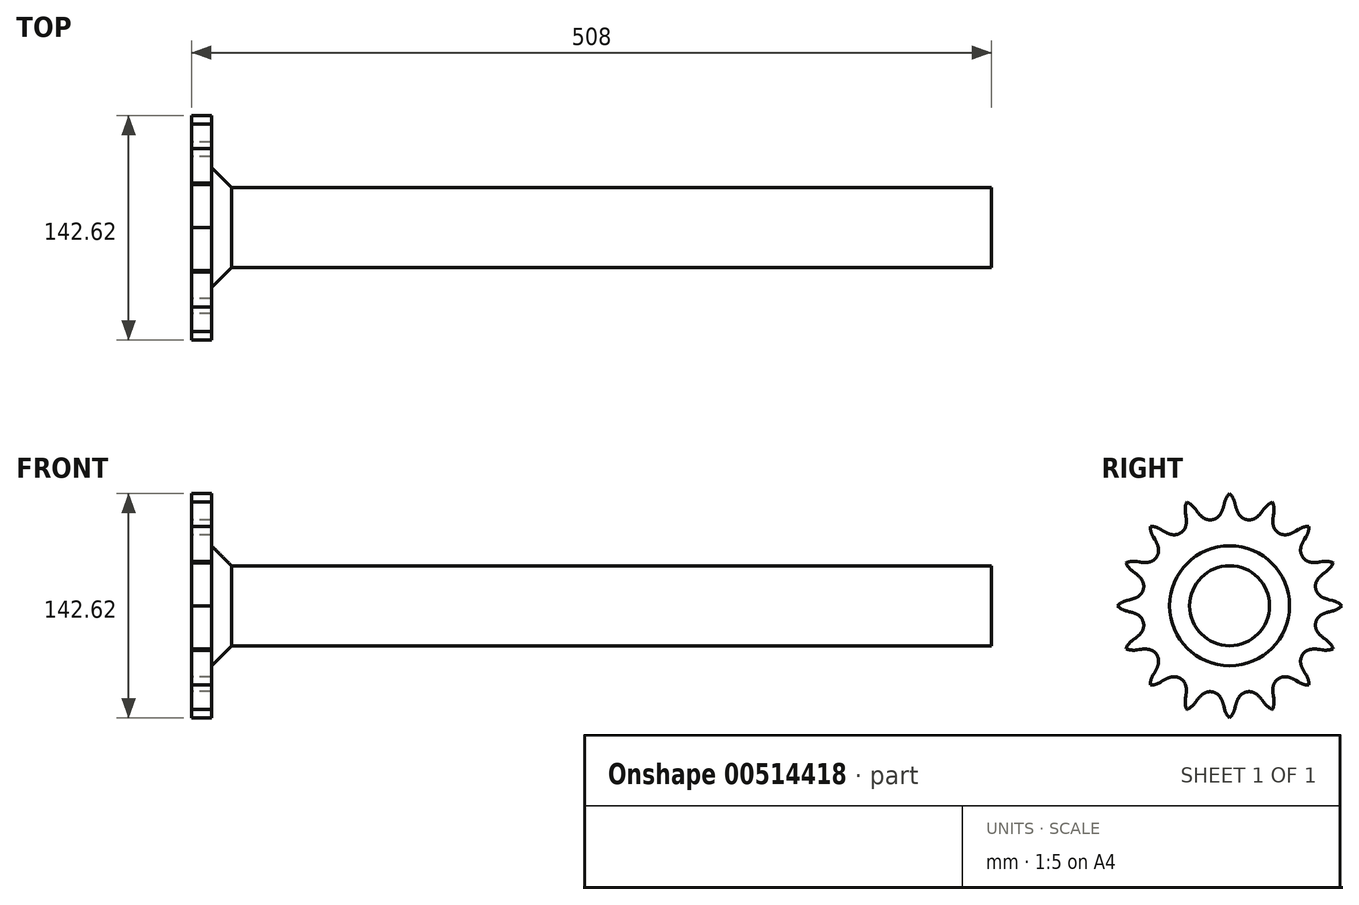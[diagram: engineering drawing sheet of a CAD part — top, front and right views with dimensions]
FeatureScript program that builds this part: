
annotation { "Feature Type Name" : "Feature", "Feature Type Description" : "" }
export const myFeature = defineFeature(function(context is Context, id is Id, definition is map)
    precondition{}
    {
        {
            var Q0;
            Q0=qCreatedBy(makeId("Front.planeOp"),FACE);
            var sketch = newSketch(context, id + "F0", { "sketchPlane" : qUnion([Q0])});
            skLineSegment(sketch, "E0", {"start": v(0, 0) * mm, "end": v(55.03, 0) * mm, "construction": true});
            skLineSegment(sketch, "E1.bottom", {"start": v(0, 25.4) * mm, "end": v(12.7, 25.4) * mm});
            skLineSegment(sketch, "E1.top", {"start": v(0, 76.2) * mm, "end": v(12.7, 76.2) * mm});
            skLineSegment(sketch, "E1.left", {"start": v(0, 25.4) * mm, "end": v(0, 76.2) * mm});
            skLineSegment(sketch, "E1.right", {"start": v(12.7, 25.4) * mm, "end": v(12.7, 76.2) * mm});
            skLineSegment(sketch, "E2.MirrorCS", {"start": v(12.7, -25.4) * mm, "end": v(12.7, -76.2) * mm});
            skLineSegment(sketch, "E3.MirrorCS", {"start": v(0, -25.4) * mm, "end": v(0, -76.2) * mm});
            skLineSegment(sketch, "E4.MirrorCS", {"start": v(0, -76.2) * mm, "end": v(12.7, -76.2) * mm});
            skLineSegment(sketch, "E5.MirrorCS", {"start": v(0, -25.4) * mm, "end": v(12.7, -25.4) * mm});
            skLineSegment(sketch, "E6.bottom", {"start": v(0, 38.1) * mm, "end": v(25.4, 38.1) * mm});
            skLineSegment(sketch, "E6.top", {"start": v(0, 25.4) * mm, "end": v(25.4, 25.4) * mm});
            skLineSegment(sketch, "E6.left", {"start": v(0, 38.1) * mm, "end": v(0, 25.4) * mm});
            skLineSegment(sketch, "E6.right", {"start": v(25.4, 38.1) * mm, "end": v(25.4, 25.4) * mm});
            skLineSegment(sketch, "E7.MirrorCS", {"start": v(25.4, -38.1) * mm, "end": v(25.4, -25.4) * mm});
            skLineSegment(sketch, "E8.MirrorCS", {"start": v(0, -38.1) * mm, "end": v(0, -25.4) * mm});
            skLineSegment(sketch, "E9.MirrorCS", {"start": v(0, -25.4) * mm, "end": v(25.4, -25.4) * mm});
            skLineSegment(sketch, "E10.MirrorCS", {"start": v(0, -38.1) * mm, "end": v(25.4, -38.1) * mm});
            skSolve(sketch);
        }
        {
            var Q0;
            Q0 = qSketchRegion(id + "F0", true);
            var Q1;
            Q1=sQuery(id+"F0.wireOp",EDGE,"E0");
            revolve(context, id + "F1", {"entities" : qUnion([Q0]), "axis" : qUnion([Q1]), "revolveType" : RevolveType.FULL});
        }
        {
            var Q0;
            Q0=makeQuery(id+"F1.opRevolve","SWEPT_FACE",FACE,{"disambiguationData":[OSD([sQuery(id+"F0.wireOp",EDGE,"E3.MirrorCS"),sQuery(id+"F0.wireOp",EDGE,"E8.MirrorCS")])]});
            var sketch = newSketch(context, id + "F2", { "sketchPlane" : qUnion([Q0])});
            skCircle(sketch, "E11", {"center": v(0, 0) * mm, "radius": 25.4 * mm});
            skSolve(sketch);
        }
        {
            var Q0;
            Q0=makeQuery(id+"F2.imprint","IMPRINT",FACE,{"disambiguationData":[TD([[makeQuery(id+"F2.imprint","IMPRINT",EDGE,{"derivedFrom":sQuery(id+"F2.wireOp",EDGE,"E11")}),1.0]])]});
            extrude(context, id + "F3", {"entities" : qUnion([Q0]), "oppositeDirection" : true, "depth" : 508 * mm, "offsetDistance" : 25.4 * mm});
        }
        {
            var Q0;
            Q0=makeQuery(id+"F3.opExtrude","SWEPT_BODY",BODY,{"disambiguationData":[OSD([sQuery(id+"F2.wireOp",EDGE,"E11")])]});
            var Q1;
            Q1=makeQuery(id+"F1.opRevolve","SWEPT_BODY",BODY,{"disambiguationData":[OSD([sQuery(id+"F0.wireOp",EDGE,"E2.MirrorCS"),sQuery(id+"F0.wireOp",EDGE,"E3.MirrorCS"),sQuery(id+"F0.wireOp",EDGE,"E4.MirrorCS"),sQuery(id+"F0.wireOp",EDGE,"E7.MirrorCS"),sQuery(id+"F0.wireOp",EDGE,"E8.MirrorCS"),sQuery(id+"F0.wireOp",EDGE,"E9.MirrorCS"),sQuery(id+"F0.wireOp",EDGE,"E10.MirrorCS")])]});
            var Q2;
            Q2=makeQuery(id+"F1.opRevolve","SWEPT_BODY",BODY,{"disambiguationData":[OSD([sQuery(id+"F0.wireOp",EDGE,"E6.bottom"),sQuery(id+"F0.wireOp",EDGE,"E6.top"),sQuery(id+"F0.wireOp",EDGE,"E6.right"),sQuery(id+"F0.wireOp",EDGE,"E1.bottom"),sQuery(id+"F0.wireOp",EDGE,"E1.top"),sQuery(id+"F0.wireOp",EDGE,"E1.left"),sQuery(id+"F0.wireOp",EDGE,"E1.right")])]});
            booleanBodies(context, id + "F4", {"operationType" : BooleanOperationType.UNION, "tools" : qUnion([Q0, Q1, Q2])});
        }
        {
            var Q0;
            Q0=makeQuery(id+"F4.opBoolean","MERGE",FACE,{"derivedFrom":[makeQuery(id+"F1.opRevolve","SWEPT_FACE",FACE,{"disambiguationData":[OSD([sQuery(id+"F0.wireOp",EDGE,"E3.MirrorCS"),sQuery(id+"F0.wireOp",EDGE,"E8.MirrorCS")])]}),makeQuery(id+"F3.opExtrude","CAP_FACE",FACE,{"disambiguationData":[OSD([sQuery(id+"F2.wireOp",EDGE,"E11")])],"isStart":true})]});
            var sketch = newSketch(context, id + "F5", { "sketchPlane" : qUnion([Q0])});
            skCircle(sketch, "E12", {"center": v(0, 0) * mm, "radius": 63.5 * mm, "construction": true});
            skLineSegment(sketch, "E13", {"start": v(0, 0) * mm, "end": v(12.39, 62.28) * mm, "construction": true});
            skLineSegment(sketch, "E14", {"start": v(12.39, 62.28) * mm, "end": v(48.32, 55.13) * mm, "construction": true});
            skLineSegment(sketch, "E15", {"start": v(48.32, 55.13) * mm, "end": v(12.39, 62.28) * mm, "construction": true});
            skLineSegment(sketch, "E16", {"start": v(12.39, 62.28) * mm, "end": v(23.46, 68.05) * mm, "construction": true});
            skLineSegment(sketch, "E17", {"start": v(23.46, 68.05) * mm, "end": v(3.77, 63.5) * mm, "construction": true});
            skLineSegment(sketch, "E18", {"start": v(3.77, 63.5) * mm, "end": v(3.38, 65.16) * mm});
            skLineSegment(sketch, "E19", {"start": v(0, 71.3) * mm, "end": v(0, 0) * mm, "construction": true});
            skArc(sketch, "E20", {"start": v(0, 71.3) * mm, "mid": v(-20.41, 56.07) * mm, "end": v(3.38, 65.16) * mm, "construction": true});
            skLineSegment(sketch, "E21", {"start": v(2.91, 11.35) * mm, "end": v(2.91, 11.35) * mm});
            skArc(sketch, "E22", {"start": v(3.38, 65.16) * mm, "mid": v(2.12, 68.47) * mm, "end": v(0, 71.3) * mm});
            skArc(sketch, "E23", {"start": v(3.77, 63.5) * mm, "mid": v(4.5, 61.05) * mm, "end": v(5.53, 58.71) * mm});
            skArc(sketch, "E24", {"start": v(5.53, 58.71) * mm, "mid": v(42.43, 75.04) * mm, "end": v(3.77, 63.5) * mm, "construction": true});
            skArc(sketch, "E25.MirrorCS", {"start": v(20.82, 60.1) * mm, "mid": v(19.2, 58.12) * mm, "end": v(17.36, 56.36) * mm});
            skArc(sketch, "E26.MirrorCS", {"start": v(21.81, 61.5) * mm, "mid": v(24.25, 64.07) * mm, "end": v(27.29, 65.88) * mm});
            skLineSegment(sketch, "E27.MirrorCS", {"start": v(20.82, 60.1) * mm, "end": v(21.81, 61.5) * mm});
            skArc(sketch, "E28", {"start": v(5.53, 58.71) * mm, "mid": v(10.88, 54.7) * mm, "end": v(17.36, 56.36) * mm});
            skArc(sketch, "E29", {"start": v(17.36, 56.36) * mm, "mid": v(13.9, 69.86) * mm, "end": v(5.53, 58.71) * mm, "construction": true});
            skLineSegment(sketch, "E30.0", {"start": v(-9.15, 62.27) * mm, "end": v(11.57, 58.15) * mm, "construction": true});
            skLineSegment(sketch, "E30.1", {"start": v(11.57, 58.15) * mm, "end": v(12.39, 62.28) * mm, "construction": true});
            skArc(sketch, "E31.1.0", {"start": v(-20.82, 60.1) * mm, "mid": v(-19.2, 58.12) * mm, "end": v(-17.36, 56.36) * mm});
            skArc(sketch, "E31.1.1", {"start": v(-21.81, 61.5) * mm, "mid": v(-24.25, 64.07) * mm, "end": v(-27.29, 65.88) * mm});
            skArc(sketch, "E31.1.2", {"start": v(-17.36, 56.36) * mm, "mid": v(-10.88, 54.7) * mm, "end": v(-5.53, 58.71) * mm});
            skArc(sketch, "E31.1.3", {"start": v(-3.77, 63.5) * mm, "mid": v(-4.5, 61.05) * mm, "end": v(-5.53, 58.71) * mm});
            skArc(sketch, "E31.1.4", {"start": v(-3.38, 65.16) * mm, "mid": v(-2.12, 68.47) * mm, "end": v(0, 71.3) * mm});
            skLineSegment(sketch, "E31.1.5", {"start": v(-3.77, 63.5) * mm, "end": v(-3.38, 65.16) * mm});
            skLineSegment(sketch, "E31.1.6", {"start": v(-20.82, 60.1) * mm, "end": v(-21.81, 61.5) * mm});
            skArc(sketch, "E31.2.0", {"start": v(-42.24, 47.56) * mm, "mid": v(-39.99, 46.35) * mm, "end": v(-37.6, 45.43) * mm});
            skArc(sketch, "E31.2.1", {"start": v(-43.69, 48.47) * mm, "mid": v(-46.92, 49.91) * mm, "end": v(-50.42, 50.42) * mm});
            skArc(sketch, "E31.2.2", {"start": v(-37.6, 45.43) * mm, "mid": v(-30.98, 46.37) * mm, "end": v(-27.58, 52.12) * mm});
            skArc(sketch, "E31.2.3", {"start": v(-27.78, 57.22) * mm, "mid": v(-27.52, 54.68) * mm, "end": v(-27.58, 52.12) * mm});
            skArc(sketch, "E31.2.4", {"start": v(-28.06, 58.9) * mm, "mid": v(-28.16, 62.45) * mm, "end": v(-27.29, 65.88) * mm});
            skLineSegment(sketch, "E31.2.5", {"start": v(-27.78, 57.22) * mm, "end": v(-28.06, 58.9) * mm});
            skLineSegment(sketch, "E31.2.6", {"start": v(-42.24, 47.56) * mm, "end": v(-43.69, 48.47) * mm});
            skArc(sketch, "E31.3.0", {"start": v(-57.22, 27.78) * mm, "mid": v(-54.68, 27.52) * mm, "end": v(-52.12, 27.58) * mm});
            skArc(sketch, "E31.3.1", {"start": v(-58.9, 28.06) * mm, "mid": v(-62.45, 28.16) * mm, "end": v(-65.88, 27.29) * mm});
            skArc(sketch, "E31.3.2", {"start": v(-52.12, 27.58) * mm, "mid": v(-46.37, 30.98) * mm, "end": v(-45.43, 37.6) * mm});
            skArc(sketch, "E31.3.3", {"start": v(-47.56, 42.24) * mm, "mid": v(-46.35, 39.99) * mm, "end": v(-45.43, 37.6) * mm});
            skArc(sketch, "E31.3.4", {"start": v(-48.47, 43.69) * mm, "mid": v(-49.91, 46.92) * mm, "end": v(-50.42, 50.42) * mm});
            skLineSegment(sketch, "E31.3.5", {"start": v(-47.56, 42.24) * mm, "end": v(-48.47, 43.69) * mm});
            skLineSegment(sketch, "E31.3.6", {"start": v(-57.22, 27.78) * mm, "end": v(-58.9, 28.06) * mm});
            skArc(sketch, "E31.4.0", {"start": v(-63.5, 3.77) * mm, "mid": v(-61.05, 4.5) * mm, "end": v(-58.71, 5.53) * mm});
            skArc(sketch, "E31.4.1", {"start": v(-65.16, 3.38) * mm, "mid": v(-68.47, 2.12) * mm, "end": v(-71.3, 0) * mm});
            skArc(sketch, "E31.4.2", {"start": v(-58.71, 5.53) * mm, "mid": v(-54.7, 10.88) * mm, "end": v(-56.36, 17.36) * mm});
            skArc(sketch, "E31.4.3", {"start": v(-60.1, 20.82) * mm, "mid": v(-58.12, 19.2) * mm, "end": v(-56.36, 17.36) * mm});
            skArc(sketch, "E31.4.4", {"start": v(-61.5, 21.81) * mm, "mid": v(-64.07, 24.25) * mm, "end": v(-65.88, 27.29) * mm});
            skLineSegment(sketch, "E31.4.5", {"start": v(-60.1, 20.82) * mm, "end": v(-61.5, 21.81) * mm});
            skLineSegment(sketch, "E31.4.6", {"start": v(-63.5, 3.77) * mm, "end": v(-65.16, 3.38) * mm});
            skArc(sketch, "E31.5.0", {"start": v(-60.1, -20.82) * mm, "mid": v(-58.12, -19.2) * mm, "end": v(-56.36, -17.36) * mm});
            skArc(sketch, "E31.5.1", {"start": v(-61.5, -21.81) * mm, "mid": v(-64.07, -24.25) * mm, "end": v(-65.88, -27.29) * mm});
            skArc(sketch, "E31.5.2", {"start": v(-56.36, -17.36) * mm, "mid": v(-54.7, -10.88) * mm, "end": v(-58.71, -5.53) * mm});
            skArc(sketch, "E31.5.3", {"start": v(-63.5, -3.77) * mm, "mid": v(-61.05, -4.5) * mm, "end": v(-58.71, -5.53) * mm});
            skArc(sketch, "E31.5.4", {"start": v(-65.16, -3.38) * mm, "mid": v(-68.47, -2.12) * mm, "end": v(-71.3, 0) * mm});
            skLineSegment(sketch, "E31.5.5", {"start": v(-63.5, -3.77) * mm, "end": v(-65.16, -3.38) * mm});
            skLineSegment(sketch, "E31.5.6", {"start": v(-60.1, -20.82) * mm, "end": v(-61.5, -21.81) * mm});
            skArc(sketch, "E31.6.0", {"start": v(-47.56, -42.24) * mm, "mid": v(-46.35, -39.99) * mm, "end": v(-45.43, -37.6) * mm});
            skArc(sketch, "E31.6.1", {"start": v(-48.47, -43.69) * mm, "mid": v(-49.91, -46.92) * mm, "end": v(-50.42, -50.42) * mm});
            skArc(sketch, "E31.6.2", {"start": v(-45.43, -37.6) * mm, "mid": v(-46.37, -30.98) * mm, "end": v(-52.12, -27.58) * mm});
            skArc(sketch, "E31.6.3", {"start": v(-57.22, -27.78) * mm, "mid": v(-54.68, -27.52) * mm, "end": v(-52.12, -27.58) * mm});
            skArc(sketch, "E31.6.4", {"start": v(-58.9, -28.06) * mm, "mid": v(-62.45, -28.16) * mm, "end": v(-65.88, -27.29) * mm});
            skLineSegment(sketch, "E31.6.5", {"start": v(-57.22, -27.78) * mm, "end": v(-58.9, -28.06) * mm});
            skLineSegment(sketch, "E31.6.6", {"start": v(-47.56, -42.24) * mm, "end": v(-48.47, -43.69) * mm});
            skArc(sketch, "E31.7.0", {"start": v(-27.78, -57.22) * mm, "mid": v(-27.52, -54.68) * mm, "end": v(-27.58, -52.12) * mm});
            skArc(sketch, "E31.7.1", {"start": v(-28.06, -58.9) * mm, "mid": v(-28.16, -62.45) * mm, "end": v(-27.29, -65.88) * mm});
            skArc(sketch, "E31.7.2", {"start": v(-27.58, -52.12) * mm, "mid": v(-30.98, -46.37) * mm, "end": v(-37.6, -45.43) * mm});
            skArc(sketch, "E31.7.3", {"start": v(-42.24, -47.56) * mm, "mid": v(-39.99, -46.35) * mm, "end": v(-37.6, -45.43) * mm});
            skArc(sketch, "E31.7.4", {"start": v(-43.69, -48.47) * mm, "mid": v(-46.92, -49.91) * mm, "end": v(-50.42, -50.42) * mm});
            skLineSegment(sketch, "E31.7.5", {"start": v(-42.24, -47.56) * mm, "end": v(-43.69, -48.47) * mm});
            skLineSegment(sketch, "E31.7.6", {"start": v(-27.78, -57.22) * mm, "end": v(-28.06, -58.9) * mm});
            skArc(sketch, "E31.8.0", {"start": v(-3.77, -63.5) * mm, "mid": v(-4.5, -61.05) * mm, "end": v(-5.53, -58.71) * mm});
            skArc(sketch, "E31.8.1", {"start": v(-3.38, -65.16) * mm, "mid": v(-2.12, -68.47) * mm, "end": v(0, -71.3) * mm});
            skArc(sketch, "E31.8.2", {"start": v(-5.53, -58.71) * mm, "mid": v(-10.88, -54.7) * mm, "end": v(-17.36, -56.36) * mm});
            skArc(sketch, "E31.8.3", {"start": v(-20.82, -60.1) * mm, "mid": v(-19.2, -58.12) * mm, "end": v(-17.36, -56.36) * mm});
            skArc(sketch, "E31.8.4", {"start": v(-21.81, -61.5) * mm, "mid": v(-24.25, -64.07) * mm, "end": v(-27.29, -65.88) * mm});
            skLineSegment(sketch, "E31.8.5", {"start": v(-20.82, -60.1) * mm, "end": v(-21.81, -61.5) * mm});
            skLineSegment(sketch, "E31.8.6", {"start": v(-3.77, -63.5) * mm, "end": v(-3.38, -65.16) * mm});
            skArc(sketch, "E31.9.0", {"start": v(20.82, -60.1) * mm, "mid": v(19.2, -58.12) * mm, "end": v(17.36, -56.36) * mm});
            skArc(sketch, "E31.9.1", {"start": v(21.81, -61.5) * mm, "mid": v(24.25, -64.07) * mm, "end": v(27.29, -65.88) * mm});
            skArc(sketch, "E31.9.2", {"start": v(17.36, -56.36) * mm, "mid": v(10.88, -54.7) * mm, "end": v(5.53, -58.71) * mm});
            skArc(sketch, "E31.9.3", {"start": v(3.77, -63.5) * mm, "mid": v(4.5, -61.05) * mm, "end": v(5.53, -58.71) * mm});
            skArc(sketch, "E31.9.4", {"start": v(3.38, -65.16) * mm, "mid": v(2.12, -68.47) * mm, "end": v(0, -71.3) * mm});
            skLineSegment(sketch, "E31.9.5", {"start": v(3.77, -63.5) * mm, "end": v(3.38, -65.16) * mm});
            skLineSegment(sketch, "E31.9.6", {"start": v(20.82, -60.1) * mm, "end": v(21.81, -61.5) * mm});
            skArc(sketch, "E31.10.0", {"start": v(42.24, -47.56) * mm, "mid": v(39.99, -46.35) * mm, "end": v(37.6, -45.43) * mm});
            skArc(sketch, "E31.10.1", {"start": v(43.69, -48.47) * mm, "mid": v(46.92, -49.91) * mm, "end": v(50.42, -50.42) * mm});
            skArc(sketch, "E31.10.2", {"start": v(37.6, -45.43) * mm, "mid": v(30.98, -46.37) * mm, "end": v(27.58, -52.12) * mm});
            skArc(sketch, "E31.10.3", {"start": v(27.78, -57.22) * mm, "mid": v(27.52, -54.68) * mm, "end": v(27.58, -52.12) * mm});
            skArc(sketch, "E31.10.4", {"start": v(28.06, -58.9) * mm, "mid": v(28.16, -62.45) * mm, "end": v(27.29, -65.88) * mm});
            skLineSegment(sketch, "E31.10.5", {"start": v(27.78, -57.22) * mm, "end": v(28.06, -58.9) * mm});
            skLineSegment(sketch, "E31.10.6", {"start": v(42.24, -47.56) * mm, "end": v(43.69, -48.47) * mm});
            skArc(sketch, "E31.11.0", {"start": v(57.22, -27.78) * mm, "mid": v(54.68, -27.52) * mm, "end": v(52.12, -27.58) * mm});
            skArc(sketch, "E31.11.1", {"start": v(58.9, -28.06) * mm, "mid": v(62.45, -28.16) * mm, "end": v(65.88, -27.29) * mm});
            skArc(sketch, "E31.11.2", {"start": v(52.12, -27.58) * mm, "mid": v(46.37, -30.98) * mm, "end": v(45.43, -37.6) * mm});
            skArc(sketch, "E31.11.3", {"start": v(47.56, -42.24) * mm, "mid": v(46.35, -39.99) * mm, "end": v(45.43, -37.6) * mm});
            skArc(sketch, "E31.11.4", {"start": v(48.47, -43.69) * mm, "mid": v(49.91, -46.92) * mm, "end": v(50.42, -50.42) * mm});
            skLineSegment(sketch, "E31.11.5", {"start": v(47.56, -42.24) * mm, "end": v(48.47, -43.69) * mm});
            skLineSegment(sketch, "E31.11.6", {"start": v(57.22, -27.78) * mm, "end": v(58.9, -28.06) * mm});
            skArc(sketch, "E31.12.0", {"start": v(63.5, -3.77) * mm, "mid": v(61.05, -4.5) * mm, "end": v(58.71, -5.53) * mm});
            skArc(sketch, "E31.12.1", {"start": v(65.16, -3.38) * mm, "mid": v(68.47, -2.12) * mm, "end": v(71.3, 0) * mm});
            skArc(sketch, "E31.12.2", {"start": v(58.71, -5.53) * mm, "mid": v(54.7, -10.88) * mm, "end": v(56.36, -17.36) * mm});
            skArc(sketch, "E31.12.3", {"start": v(60.1, -20.82) * mm, "mid": v(58.12, -19.2) * mm, "end": v(56.36, -17.36) * mm});
            skArc(sketch, "E31.12.4", {"start": v(61.5, -21.81) * mm, "mid": v(64.07, -24.25) * mm, "end": v(65.88, -27.29) * mm});
            skLineSegment(sketch, "E31.12.5", {"start": v(60.1, -20.82) * mm, "end": v(61.5, -21.81) * mm});
            skLineSegment(sketch, "E31.12.6", {"start": v(63.5, -3.77) * mm, "end": v(65.16, -3.38) * mm});
            skArc(sketch, "E31.13.0", {"start": v(60.1, 20.82) * mm, "mid": v(58.12, 19.2) * mm, "end": v(56.36, 17.36) * mm});
            skArc(sketch, "E31.13.1", {"start": v(61.5, 21.81) * mm, "mid": v(64.07, 24.25) * mm, "end": v(65.88, 27.29) * mm});
            skArc(sketch, "E31.13.2", {"start": v(56.36, 17.36) * mm, "mid": v(54.7, 10.88) * mm, "end": v(58.71, 5.53) * mm});
            skArc(sketch, "E31.13.3", {"start": v(63.5, 3.77) * mm, "mid": v(61.05, 4.5) * mm, "end": v(58.71, 5.53) * mm});
            skArc(sketch, "E31.13.4", {"start": v(65.16, 3.38) * mm, "mid": v(68.47, 2.12) * mm, "end": v(71.3, 0) * mm});
            skLineSegment(sketch, "E31.13.5", {"start": v(63.5, 3.77) * mm, "end": v(65.16, 3.38) * mm});
            skLineSegment(sketch, "E31.13.6", {"start": v(60.1, 20.82) * mm, "end": v(61.5, 21.81) * mm});
            skArc(sketch, "E31.14.0", {"start": v(47.56, 42.24) * mm, "mid": v(46.35, 39.99) * mm, "end": v(45.43, 37.6) * mm});
            skArc(sketch, "E31.14.1", {"start": v(48.47, 43.69) * mm, "mid": v(49.91, 46.92) * mm, "end": v(50.42, 50.42) * mm});
            skArc(sketch, "E31.14.2", {"start": v(45.43, 37.6) * mm, "mid": v(46.37, 30.98) * mm, "end": v(52.12, 27.58) * mm});
            skArc(sketch, "E31.14.3", {"start": v(57.22, 27.78) * mm, "mid": v(54.68, 27.52) * mm, "end": v(52.12, 27.58) * mm});
            skArc(sketch, "E31.14.4", {"start": v(58.9, 28.06) * mm, "mid": v(62.45, 28.16) * mm, "end": v(65.88, 27.29) * mm});
            skLineSegment(sketch, "E31.14.5", {"start": v(57.22, 27.78) * mm, "end": v(58.9, 28.06) * mm});
            skLineSegment(sketch, "E31.14.6", {"start": v(47.56, 42.24) * mm, "end": v(48.47, 43.69) * mm});
            skArc(sketch, "E31.15.0", {"start": v(27.78, 57.22) * mm, "mid": v(27.52, 54.68) * mm, "end": v(27.58, 52.12) * mm});
            skArc(sketch, "E31.15.1", {"start": v(28.06, 58.9) * mm, "mid": v(28.16, 62.45) * mm, "end": v(27.29, 65.88) * mm});
            skArc(sketch, "E31.15.2", {"start": v(27.58, 52.12) * mm, "mid": v(30.98, 46.37) * mm, "end": v(37.6, 45.43) * mm});
            skArc(sketch, "E31.15.3", {"start": v(42.24, 47.56) * mm, "mid": v(39.99, 46.35) * mm, "end": v(37.6, 45.43) * mm});
            skArc(sketch, "E31.15.4", {"start": v(43.69, 48.47) * mm, "mid": v(46.92, 49.91) * mm, "end": v(50.42, 50.42) * mm});
            skLineSegment(sketch, "E31.15.5", {"start": v(42.24, 47.56) * mm, "end": v(43.69, 48.47) * mm});
            skLineSegment(sketch, "E31.15.6", {"start": v(27.78, 57.22) * mm, "end": v(28.06, 58.9) * mm});
            skSolve(sketch);
        }
        {
            var Q0;
            Q0=makeQuery(id+"F5.imprint","IMPRINT",FACE,{"disambiguationData":[TD([[makeQuery(id+"F5.imprint","IMPRINT",EDGE,{"derivedFrom":sQuery(id+"F5.wireOp",EDGE,"E18")}),1.0]])]});
            extrude(context, id + "F6", {"entities" : qUnion([Q0]), "operationType" : NewBodyOperationType.INTERSECT, "endBound" : BoundingType.THROUGH_ALL, "oppositeDirection" : true, "depth" : 25.4 * mm, "offsetDistance" : 25.4 * mm});
        }
        {
            var Q0;
            Q0=makeQuery(id+"F1.opRevolve","SWEPT_EDGE",EDGE,{"disambiguationData":[OSD([sQuery(id+"F0.wireOp",EDGE,"E7.MirrorCS"),sQuery(id+"F0.wireOp",EDGE,"E10.MirrorCS")])]});
            chamfer(context, id + "F7", {"entities" : qUnion([Q0]), "width" : 12.7 * mm, "tangentPropagation" : true});
        }
    });
